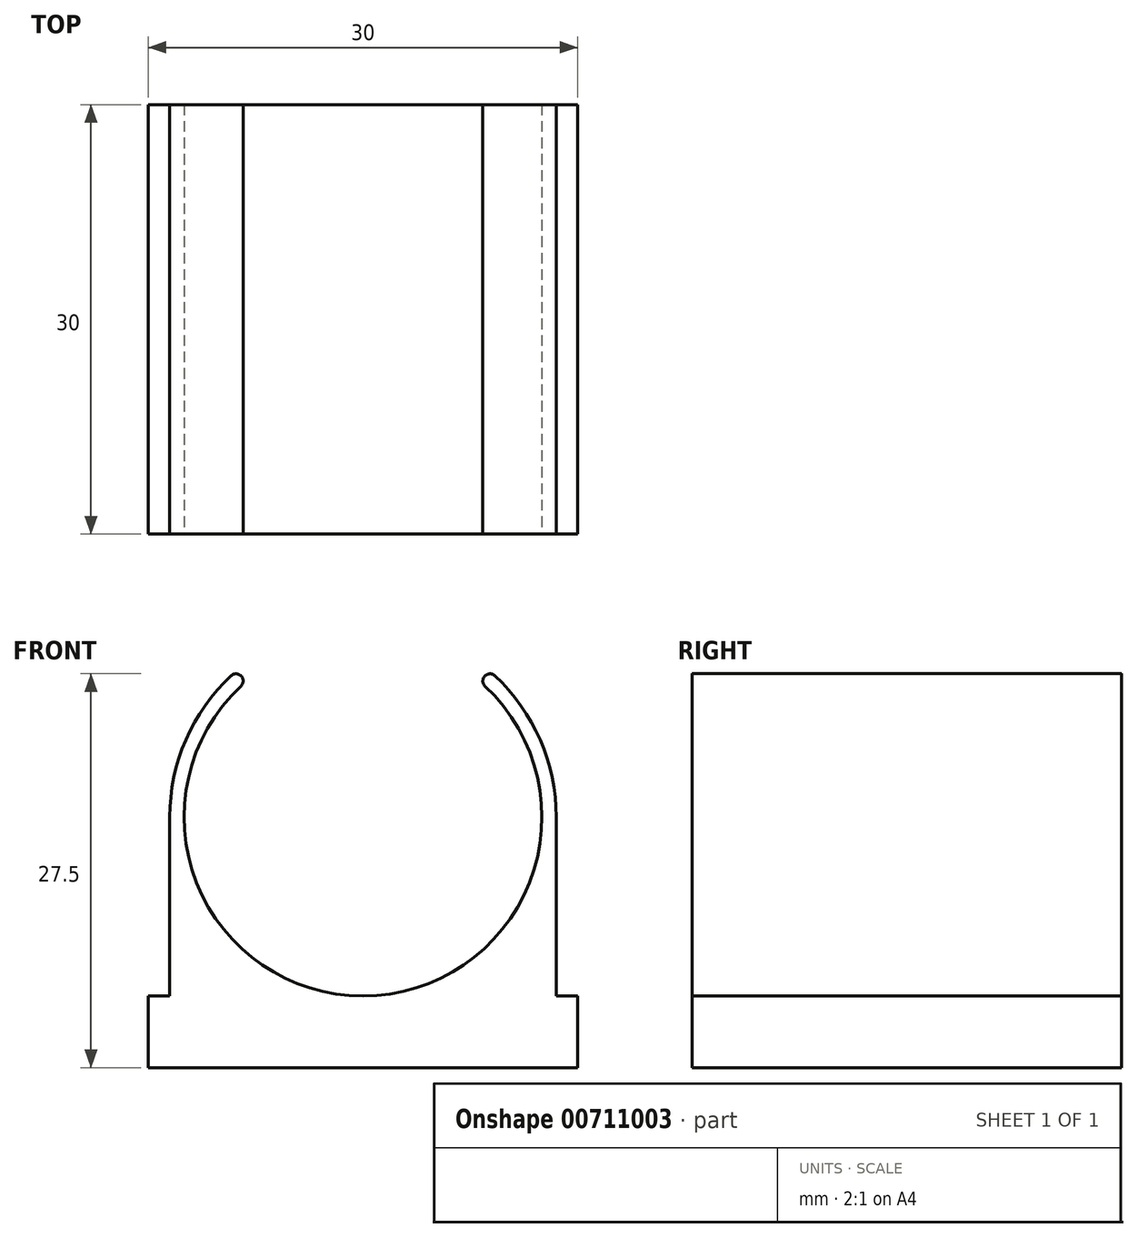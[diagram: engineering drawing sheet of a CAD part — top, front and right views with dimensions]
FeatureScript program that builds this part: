
annotation { "Feature Type Name" : "Feature", "Feature Type Description" : "" }
export const myFeature = defineFeature(function(context is Context, id is Id, definition is map)
    precondition{}
    {
        {
            var Q0;
            Q0=qCreatedBy(makeId("Front.planeOp"),FACE);
            var sketch = newSketch(context, id + "F0", { "sketchPlane" : qUnion([Q0])});
            skArc(sketch, "E0", {"start": v(-7.5, 22.5) * mm, "mid": v(0, 0) * mm, "end": v(7.5, 22.5) * mm});
            skArc(sketch, "E1", {"start": v(-9.07, 22.5) * mm, "mid": v(-12.34, 17.97) * mm, "end": v(-13.5, 12.5) * mm});
            skLineSegment(sketch, "E2", {"start": v(-13.5, 12.5) * mm, "end": v(-13.5, 0) * mm});
            skLineSegment(sketch, "E3", {"start": v(-9.07, 22.5) * mm, "end": v(9.07, 22.5) * mm});
            skLineSegment(sketch, "E4", {"start": v(13.5, 12.5) * mm, "end": v(13.5, 0) * mm});
            skLineSegment(sketch, "E5", {"start": v(13.5, 0) * mm, "end": v(-13.5, 0) * mm});
            skArc(sketch, "E6.trimOffspring", {"start": v(13.5, 12.5) * mm, "mid": v(12.34, 17.97) * mm, "end": v(9.07, 22.5) * mm});
            skSolve(sketch);
        }
        {
            var Q0;
            Q0=qCreatedBy(makeId("Top.planeOp"),FACE);
            var sketch = newSketch(context, id + "F1", { "sketchPlane" : qUnion([Q0])});
            skLineSegment(sketch, "E7.bottom", {"start": v(15, 15) * mm, "end": v(-15, 15) * mm});
            skLineSegment(sketch, "E7.top", {"start": v(15, -15) * mm, "end": v(-15, -15) * mm});
            skLineSegment(sketch, "E7.left", {"start": v(15, 15) * mm, "end": v(15, -15) * mm});
            skLineSegment(sketch, "E7.right", {"start": v(-15, 15) * mm, "end": v(-15, -15) * mm});
            skPoint(sketch, "E7.middle", {"position": v(0, 0) * mm});
            skSolve(sketch);
        }
        {
            var Q0;
            Q0=makeQuery(id+"F1.imprint","IMPRINT",FACE,{"disambiguationData":[TD([[makeQuery(id+"F1.imprint","IMPRINT",EDGE,{"derivedFrom":sQuery(id+"F1.wireOp",EDGE,"E7.bottom")}),1.0]])]});
            extrude(context, id + "F2", {"entities" : qUnion([Q0]), "oppositeDirection" : true, "depth" : 5 * mm, "offsetDistance" : 25 * mm});
        }
        {
            var Q0;
            {var subQ3=sQuery(id+"F0.wireOp",EDGE,"E1");Q0=makeQuery(id+"F0.imprint","IMPRINT",FACE,{"disambiguationData":[TD([[makeQuery(id+"F0.imprint","IMPRINT",EDGE,{"derivedFrom":subQ3}),1.0]])]});}
            var Q1;
            {var subQ1=sQuery(id+"F0.wireOp",EDGE,"E4");Q1=makeQuery(id+"F0.imprint","IMPRINT",FACE,{"disambiguationData":[TD([[makeQuery(id+"F0.imprint","IMPRINT",EDGE,{"derivedFrom":subQ1}),-1.0]])]});}
            extrude(context, id + "F3", {"entities" : qUnion([Q0, Q1]), "operationType" : NewBodyOperationType.ADD, "endBound" : BoundingType.SYMMETRIC, "oppositeDirection" : true, "depth" : 30 * mm, "offsetDistance" : 25 * mm});
        }
        {
            var Q0;
            {var subQ0=sQuery(id+"F0.wireOp",EDGE,"E3");var subQ1=sQuery(id+"F0.wireOp",EDGE,"E0");Q0=makeQuery(id+"F3.opExtrude","SWEPT_EDGE",EDGE,{"disambiguationData":[OSD([subQ1,subQ0]),TDD([makeQuery(id+"F0.imprint","INTERSECT",VERTEX,{"disambiguationData":[OD(0.0)],"derivedFrom":[subQ1,subQ0]})])]});}
            var Q1;
            Q1=makeQuery(id+"F3.opExtrude","SWEPT_EDGE",EDGE,{"disambiguationData":[OSD([sQuery(id+"F0.wireOp",EDGE,"E3"),sQuery(id+"F0.wireOp",EDGE,"E6.trimOffspring")])]});
            var Q2;
            {var subQ0=sQuery(id+"F0.wireOp",EDGE,"E3");var subQ1=sQuery(id+"F0.wireOp",EDGE,"E0");Q2=makeQuery(id+"F3.opExtrude","SWEPT_EDGE",EDGE,{"disambiguationData":[OSD([subQ1,subQ0]),TDD([makeQuery(id+"F0.imprint","INTERSECT",VERTEX,{"disambiguationData":[OD(1.0)],"derivedFrom":[subQ1,subQ0]})])]});}
            var Q3;
            Q3=makeQuery(id+"F3.opExtrude","SWEPT_EDGE",EDGE,{"disambiguationData":[OSD([sQuery(id+"F0.wireOp",EDGE,"E1"),sQuery(id+"F0.wireOp",EDGE,"E3")])]});
            fillet(context, id + "F4", {"entities" : qUnion([Q0, Q1, Q2, Q3]), "radius" : 0.5 * mm, "tangentPropagation" : true, "allowEdgeOverflow" : false});
        }
    });
